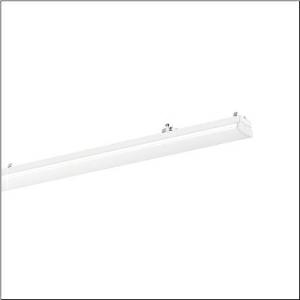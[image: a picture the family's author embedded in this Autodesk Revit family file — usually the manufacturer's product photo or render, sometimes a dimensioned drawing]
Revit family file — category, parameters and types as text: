
# Revit family: licross_11_recessed_opal_mo_51tl1dmn495g
name_source: partatom
category: Lighting Fixtures
units: mm (PartAtom-declared; Revit-internal decimal feet)

## family parameters
Cut with Voids When Loaded = No
Host = Face
Light Source = No
Part Type = Normal
Room Calculation Point = No
Round Connector Dimension = Use Diameter
Shared = No

## types (1)
- --- (1 x LED, 9750 lm, 55.2 W, 4000K)
    Apparent Load = 55 VA
    CIE Flux Codes = 44 73 91 87 100
    Color Rendering = 80
    Color Temperature = 4000K
    Default Elevation = 1800 mm
    Description = Licross 11 recessed opal MO, luminaire insert, of sheet steel, coil coated, white, length: 1.500mm, width: 76mm, height: 87mm, LED rated luminous flux: 9.750lm, light colour: 840, SDCM (Standard Deviation of Colour Matching)MacAdam ≤ 2 SDCM (initial), control gear: ON/OFF Multilumen, with plug, 3-pole, with phase selection, mains connection: 220..240V, AC, 50/60Hz, rated input power: 55W, internal wiring halogen-free, primary optical cover: cover, of PMMA, light emission: direct with ceiling illumination distribution, primary light characteristic: symmetric, protection rating (complete): IP40, insulation class (complete): insulation class I (protective earthing), certification: CE, ENEC, VDE, UKCA, protection symbol: D if used in an environment without relevant dust loads with corresponding accessories, impact resistance: IK06, permissible ambient temperature for indoor applications: -35..+40°C, corresponds to IFS (International Featured Standards) requirements for safety and quality in the food industry, reducing of maximum allowable ambient temperature of 5°C with ceiling mounting, The light source and the operating device comply with the requirements of the Ecodesign Regulation (EU) 2019/2020 and are replaceable in accordance with this regulation, packaging unit: 1 piece
    Height = 83 mm
    Lamp = 1 x LED
    Lamp Light Flux = 9750 lm
    Lamp Power = 55.2 W
    Lamp count = 1
    Length = 1500 mm
    Luminous efficacy = 177 lm/W
    Manufacturer = Siteco
    ModVariant = No
    Model = 51TL1DMN495G
    Mounting Place = Ceiling
    Mounting Type = Pendant
    Number of Poles = 1
    OnlyDefault = Yes
    Power Factor = 1
    Product Name = Licross 11 recessed opal MO
    Product group = luminaire insert | ceiling pendant
    ProductGroupID = 901
    Protection Class = Protection class I
    Protection Degree = IP 40
    RLX_Detail_Level = 1
    RLX_Emergency_Light_Flux = 0 lm
    RLX_Emergency_Type = 0
    RLX_Emergency_Type_DB = No
    RlxData = <blob elided: 25093 chars, md5=7d609163>
    Socket = socket
    Standby Power = 0 W
    System Light Flux = 9750 lm
    System Power = 55 W
    Type Comments = factory setting: luminous flux: 100 % | (A | C | E) | 126 mA
    Type Image = l_1313666.jpg
    URL = http://relux.com
    VarID = @adj_083573
    Voltage = 0 V
    Weight = 0.00 kg
    Width = 76 mm

## geometry (parser evidence)
native form markers: Blend x4, Sweep x11
no freeform markers — native parametric forms only
